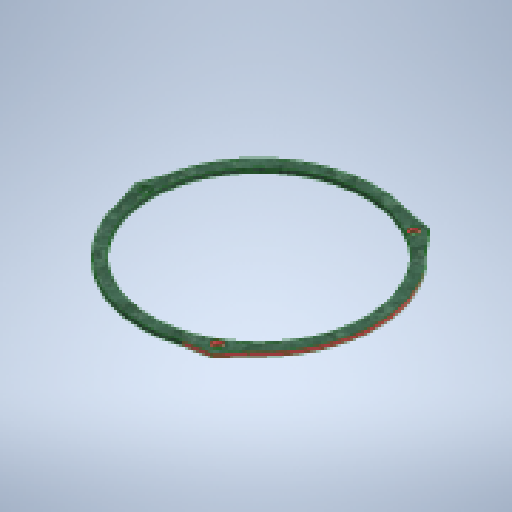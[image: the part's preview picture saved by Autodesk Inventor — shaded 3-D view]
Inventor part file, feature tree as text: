
AUTODESK INVENTOR PART (.ipt)
format: ipt  version: 2023 (Build 270158000, 158)  size: 518,144 bytes
history: native  units: mm
features: extrude x5, sketch x4, other x1, fillet x1
ambient origin geometry x8: Origin, YZ Plane, XZ Plane, XY Plane, X Axis, Y Axis, Z Axis, Center Point
bodies: Body1 (feature_tree)
feature tree (11):
  other  "Bryła1"
  extrude  "Wyciągnięcie proste1"  Depth=290.0mm
  sketch  "Szkic2"
  extrude  "Wyciągnięcie proste2"  Depth=320.0mm
  extrude  "Wyciągnięcie proste3"  Depth=6.0mm TaperAngle=0.0deg
  extrude  "Wyciągnięcie proste4"  TaperAngle=60.0deg  [1 undecoded]
  fillet  "Zaokrąglenie1"  Radius=153.5mm
  extrude  "Wyciągnięcie proste6"  Depth=153.5mm
  sketch  "Szkic1"
  sketch  "Szkic3"
  sketch  "Szkic4"
note: 1 required parameter value undecoded (feature->parameter linkage not recoverable at this tier; creation-order binding heuristic only, values carry confidence <= 0.55)
